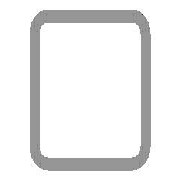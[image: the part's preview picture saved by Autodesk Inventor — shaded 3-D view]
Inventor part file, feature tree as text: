
AUTODESK INVENTOR PART (.ipt)
format: ipt  version: 2025 (Build 290162010, 162A)  size: 134,144 bytes
history: native  units: mm (DEFAULTED — no unit token found)
features: other x4, sketch x1, plane x1
ambient origin geometry x8: Origin, YZ Plane, XZ Plane, XY Plane, X Axis, Y Axis, Z Axis, Center Point
bodies: Solid1 (feature_tree), Body (feature_tree)
feature tree (6):
  parser-record x1  (decoder bookkeeping rows leaked as tree rows — omitted from the tree; the rows remain in map.json)
  other  "Driven Length"
  other  "Start Plane"
  other  "End Plane"
  sketch  "Sketch3"  dims[d3=1240.0mm d4=0.0mm d7=6.0mm d9=80.0mm d11=80.0mm d12=3.0mm d13=80.0mm d14=1320.0mm d15=40.0mm d16=40.0mm d17=90.0deg d18=1240.0mm]
  plane  "Work Plane3"
